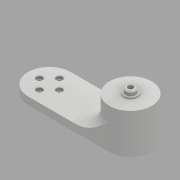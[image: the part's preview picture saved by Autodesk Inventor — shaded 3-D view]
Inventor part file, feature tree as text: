
AUTODESK INVENTOR PART (.ipt)
format: ipt  version: 2017 (Build 210142000, 142)  size: 396,800 bytes
history: native  units: mm
features: extrude x8, sketch x8, chamfer x3, hole x1, fillet x1
ambient origin geometry x8: Origin, YZ Plane, XZ Plane, XY Plane, X Axis, Y Axis, Z Axis, Center Point
bodies: Solid1 (feature_tree)
feature tree (21):
  extrude  "Extrusion1"  Depth=34.0mm
  extrude  "Extrusion2"  Depth=26.0mm TaperAngle=0.0deg
  extrude  "Extrusion3"  Depth=2.4mm
  extrude  "Extrusion4"  Depth=10.0mm TaperAngle=0.0deg
  extrude  "Extrusion5"  Depth=5.0mm
  extrude  "Extrusion6"  Depth=5.0mm
  extrude  "Extrusion7"  Depth=15.0mm
  extrude  "Extrusion8"  Depth=10.0mm
  chamfer  "Chamfer1"  Distance=3.5mm
  hole  "Hole1"  [1 undecoded]
  chamfer  "Chamfer2"  Distance=1.0mm
  fillet  "Fillet3"  Radius=8.0mm
  chamfer  "Chamfer3"  Distance=3.5mm
  sketch  "Sketch1"  dims[d1=65.0mm d2=34.0mm]
  sketch  "Sketch2"  dims[d3=6.0mm d4=0.0mm d5=26.0mm d6=0.0mm]
  sketch  "Sketch3"  dims[d7=16.0mm d8=2.4mm]
  sketch  "Sketch4"  dims[d9=40.0mm d11=360.0deg d13=10.0mm d14=0.0mm]
  sketch  "Sketch5"  dims[d15=5.0mm d16=5.0mm]
  sketch  "Sketch6"  dims[d17=5.0mm d18=5.0mm]
  sketch  "Sketch7"  dims[d19=2.0mm d20=0.0mm d22=15.0mm]
  sketch  "Sketch8"  dims[d23=18.0mm d24=0.0mm d26=7.2mm d27=3.5mm d28=0.0mm d29=11.0mm d30=1.0mm d31=0.0mm d32=8.0mm d33=3.5mm d34=0.0mm d35=1.0mm d36=2.0mm d37=45.0deg d38=10.0mm d39=10.0mm d40=4.3mm d41=6.0mm d42=4.0mm d43=2.0mm d44=90.0deg d45=8.0mm d46=20.594885mm d47=2.0mm d48=2.0mm d49=45.0deg d50=15.0mm d51=3.89998mm d52=2.0mm d53=45.0deg]
note: 1 required parameter value undecoded (feature->parameter linkage not recoverable at this tier; creation-order binding heuristic only, values carry confidence <= 0.55)
